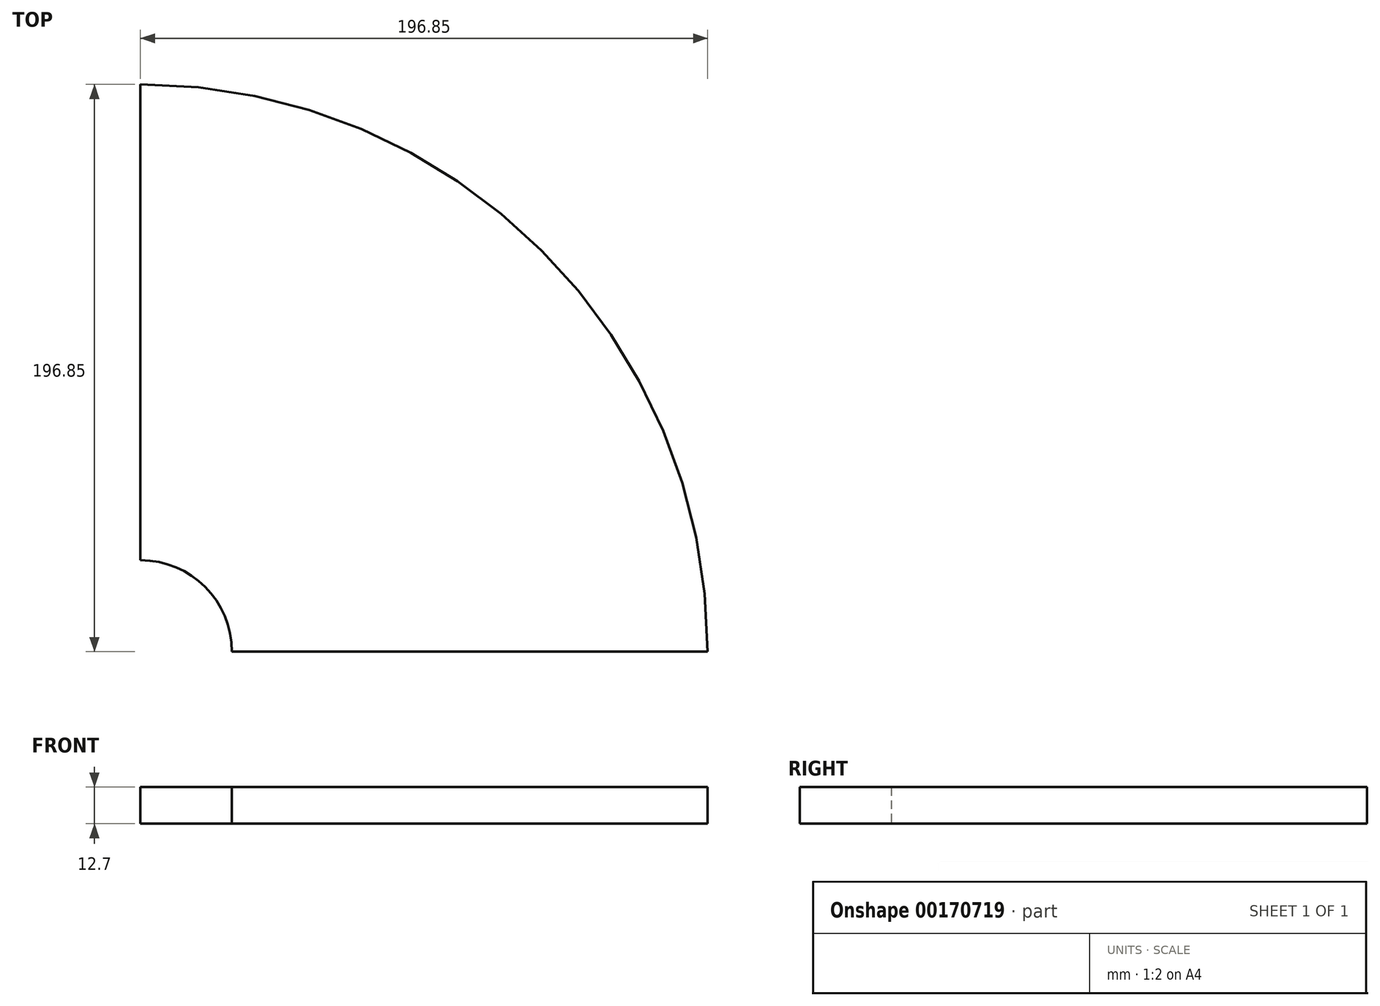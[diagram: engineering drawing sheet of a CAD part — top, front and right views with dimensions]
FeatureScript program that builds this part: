
annotation { "Feature Type Name" : "Feature", "Feature Type Description" : "" }
export const myFeature = defineFeature(function(context is Context, id is Id, definition is map)
    precondition{}
    {
        {
            var Q0;
            Q0=qCreatedBy(makeId("Top.planeOp"),FACE);
            var sketch = newSketch(context, id + "F0", { "sketchPlane" : qUnion([Q0])});
            skArc(sketch, "E0", {"start": v(31.75, 0) * mm, "mid": v(22.45, 22.45) * mm, "end": v(0, 31.75) * mm});
            skArc(sketch, "E1", {"start": v(196.85, 0) * mm, "mid": v(139.2, 139.2) * mm, "end": v(0, 196.85) * mm});
            skLineSegment(sketch, "E2", {"start": v(31.75, 0) * mm, "end": v(196.85, 0) * mm});
            skLineSegment(sketch, "E3", {"start": v(0, 31.75) * mm, "end": v(0, 196.85) * mm});
            skSolve(sketch);
        }
        {
            var Q0;
            Q0=makeQuery(id+"F0.imprint","IMPRINT",FACE,{"disambiguationData":[TD([[makeQuery(id+"F0.imprint","IMPRINT",EDGE,{"derivedFrom":sQuery(id+"F0.wireOp",EDGE,"E0")}),-1.0]])]});
            extrude(context, id + "F1", {"entities" : qUnion([Q0]), "depth" : 12.7 * mm});
        }
    });
